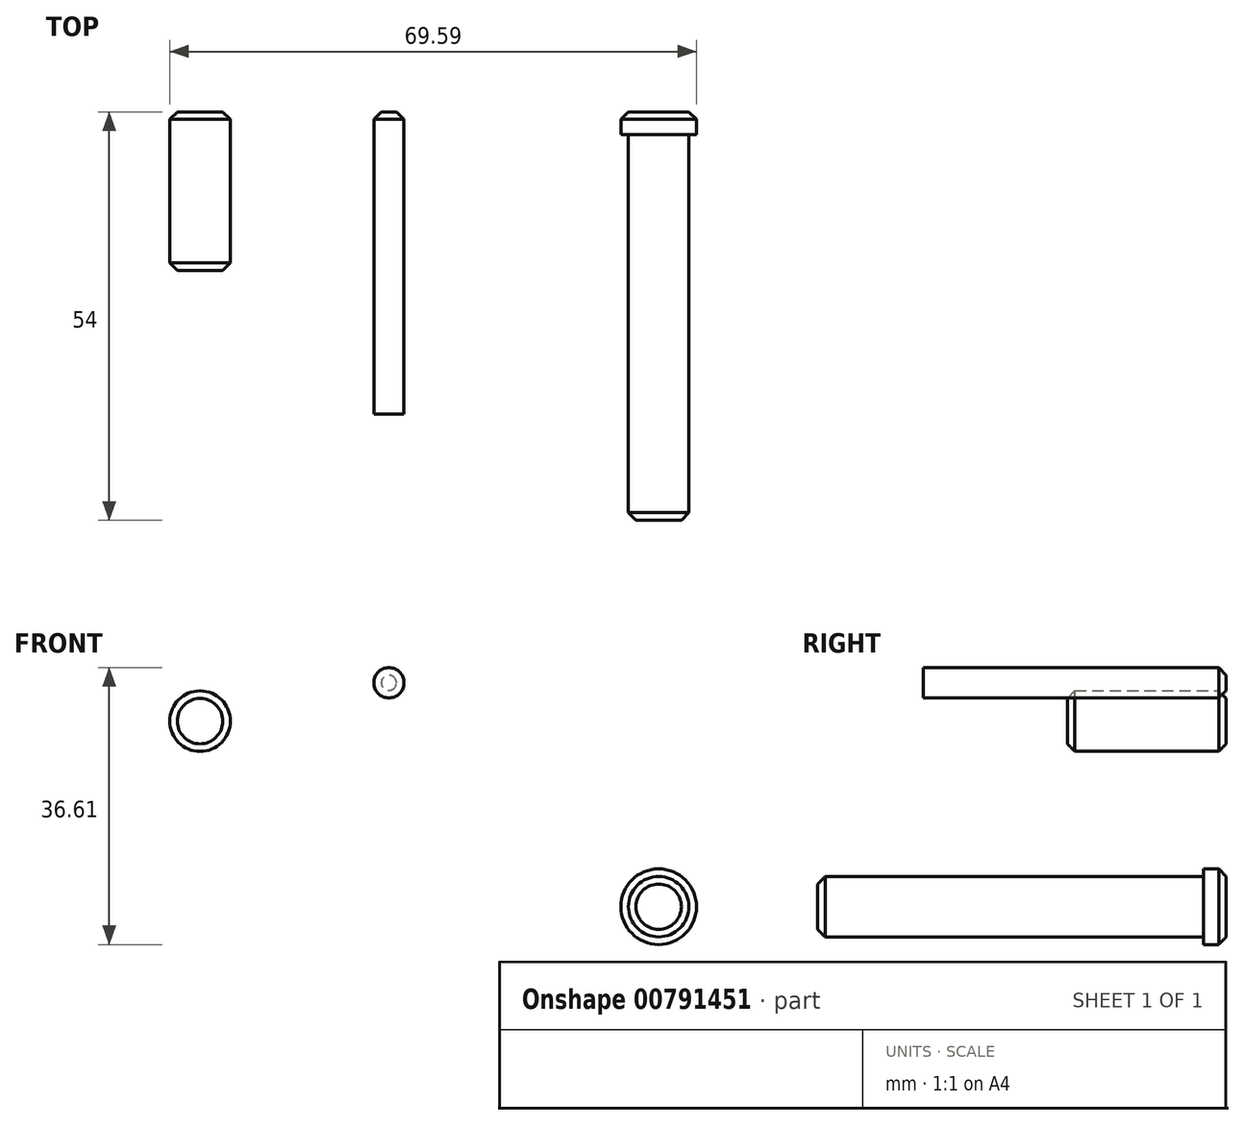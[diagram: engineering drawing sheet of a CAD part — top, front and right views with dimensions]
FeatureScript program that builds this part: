
annotation { "Feature Type Name" : "Feature", "Feature Type Description" : "" }
export const myFeature = defineFeature(function(context is Context, id is Id, definition is map)
    precondition{}
    {
        {
            var Q0;
            Q0=qCreatedBy(makeId("Front.planeOp"),FACE);
            var sketch = newSketch(context, id + "F0", { "sketchPlane" : qUnion([Q0])});
            skCircle(sketch, "E0", {"center": v(0, 0) * mm, "radius": 5 * mm});
            skSolve(sketch);
        }
        {
            var Q0;
            Q0 = qSketchRegion(id + "F0", true);
            extrude(context, id + "F1", {"entities" : qUnion([Q0]), "depth" : 3 * mm, "offsetDistance" : 25 * mm});
        }
        {
            var Q0;
            Q0=makeQuery(id+"F1.opExtrude","CAP_FACE",FACE,{"disambiguationData":[OSD([sQuery(id+"F0.wireOp",EDGE,"E0")])],"isStart":false});
            var sketch = newSketch(context, id + "F2", { "sketchPlane" : qUnion([Q0])});
            skCircle(sketch, "E1", {"center": v(0, 0) * mm, "radius": 4 * mm});
            skSolve(sketch);
        }
        {
            var Q0;
            Q0 = qSketchRegion(id + "F2", true);
            extrude(context, id + "F3", {"entities" : qUnion([Q0]), "operationType" : NewBodyOperationType.ADD, "depth" : 51 * mm, "offsetDistance" : 25 * mm});
        }
        {
            var Q0;
            Q0=qCreatedBy(makeId("Front.planeOp"),FACE);
            var sketch = newSketch(context, id + "F4", { "sketchPlane" : qUnion([Q0])});
            skCircle(sketch, "E2", {"center": v(-60.6, 24.53) * mm, "radius": 4 * mm});
            skSolve(sketch);
        }
        {
            var Q0;
            Q0 = qSketchRegion(id + "F4", true);
            extrude(context, id + "F5", {"entities" : qUnion([Q0]), "depth" : 21 * mm, "offsetDistance" : 25 * mm});
        }
        {
            var Q0;
            Q0=qCreatedBy(makeId("Front.planeOp"),FACE);
            var sketch = newSketch(context, id + "F6", { "sketchPlane" : qUnion([Q0])});
            skCircle(sketch, "E3", {"center": v(-35.64, 29.6) * mm, "radius": 2 * mm});
            skSolve(sketch);
        }
        {
            var Q0;
            Q0 = qSketchRegion(id + "F6", true);
            extrude(context, id + "F7", {"entities" : qUnion([Q0]), "depth" : 40 * mm, "offsetDistance" : 25 * mm});
        }
        {
            var Q0;
            Q0=makeQuery(id+"F1.opExtrude","CAP_EDGE",EDGE,{"disambiguationData":[OSD([sQuery(id+"F0.wireOp",EDGE,"E0")])],"isStart":true});
            var Q1;
            Q1=makeQuery(id+"F3.opExtrude","CAP_EDGE",EDGE,{"disambiguationData":[OSD([sQuery(id+"F2.wireOp",EDGE,"E1")])],"isStart":false});
            var Q2;
            Q2=makeQuery(id+"F5.opExtrude","CAP_EDGE",EDGE,{"disambiguationData":[OSD([sQuery(id+"F4.wireOp",EDGE,"E2")])],"isStart":false});
            var Q3;
            Q3=makeQuery(id+"F5.opExtrude","CAP_EDGE",EDGE,{"disambiguationData":[OSD([sQuery(id+"F4.wireOp",EDGE,"E2")])],"isStart":true});
            var Q4;
            Q4=makeQuery(id+"F7.opExtrude","CAP_EDGE",EDGE,{"disambiguationData":[OSD([sQuery(id+"F6.wireOp",EDGE,"E3")])],"isStart":true});
            chamfer(context, id + "F8", {"entities" : qUnion([Q0, Q1, Q2, Q3, Q4]), "width" : 1 * mm, "tangentPropagation" : true});
        }
    });
